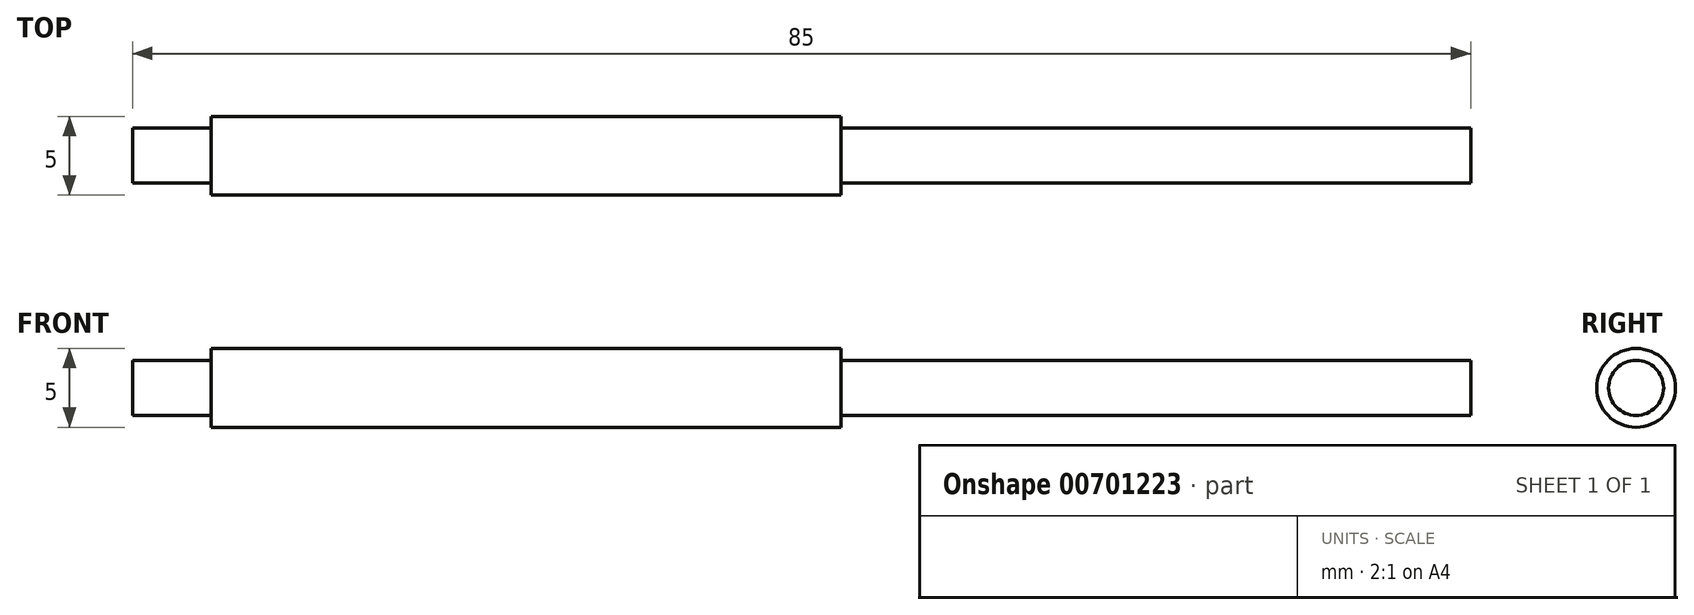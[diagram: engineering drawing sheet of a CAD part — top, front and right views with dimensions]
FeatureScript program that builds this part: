
annotation { "Feature Type Name" : "Feature", "Feature Type Description" : "" }
export const myFeature = defineFeature(function(context is Context, id is Id, definition is map)
    precondition{}
    {
        {
            var Q0;
            Q0=qCreatedBy(makeId("Top.planeOp"),FACE);
            var sketch = newSketch(context, id + "F0", { "sketchPlane" : qUnion([Q0])});
            skLineSegment(sketch, "E0.bottom", {"start": v(-20, 15) * mm, "end": v(20, 15) * mm});
            skLineSegment(sketch, "E0.top", {"start": v(-20, 0) * mm, "end": v(20, 0) * mm});
            skLineSegment(sketch, "E0.left", {"start": v(-20, 15) * mm, "end": v(-20, 0) * mm});
            skLineSegment(sketch, "E0.right", {"start": v(20, 15) * mm, "end": v(20, 0) * mm});
            skPoint(sketch, "E0.middle", {"position": v(0, 7.5) * mm});
            skSolve(sketch);
        }
        {
            var Q0;
            Q0=qSketchRegion(id+"F0",true);
            var Q1;
            Q1=sQuery(id+"F0.wireOp",EDGE,"E0.top");
            revolve(context, id + "F1", {"entities" : qUnion([Q0]), "axis" : qUnion([Q1]), "revolveType" : RevolveType.FULL});
        }
        {
            var Q0;
            Q0=makeQuery(id+"F1.opRevolve","SWEPT_FACE",FACE,{"disambiguationData":[OSD([sQuery(id+"F0.wireOp",EDGE,"E0.right")])]});
            var sketch = newSketch(context, id + "F2", { "sketchPlane" : qUnion([Q0])});
            skCircle(sketch, "E1", {"center": v(0, 0) * mm, "radius": 1.75 * mm});
            skCircle(sketch, "E2.0", {"center": v(0, 0) * mm, "radius": 15 * mm});
            skLineSegment(sketch, "E3", {"start": v(-10.07, -11.12) * mm, "end": v(-0.6, -1.65) * mm});
            skLineSegment(sketch, "E4", {"start": v(-11.13, -10.06) * mm, "end": v(-1.65, -0.58) * mm});
            skLineSegment(sketch, "E5", {"start": v(-14.98, 0.75) * mm, "end": v(-1.58, 0.75) * mm});
            skLineSegment(sketch, "E6", {"start": v(-14.98, -0.75) * mm, "end": v(-1.58, -0.75) * mm});
            skLineSegment(sketch, "E7", {"start": v(-0.75, 14.98) * mm, "end": v(-0.75, 1.58) * mm});
            skLineSegment(sketch, "E8", {"start": v(0.75, -14.98) * mm, "end": v(0.75, -1.58) * mm});
            skLineSegment(sketch, "E9.MirrorCS", {"start": v(-0.75, -14.98) * mm, "end": v(-0.75, -1.58) * mm});
            skLineSegment(sketch, "E10.MirrorCS", {"start": v(11.13, -10.06) * mm, "end": v(1.65, -0.58) * mm});
            skLineSegment(sketch, "E11.MirrorCS", {"start": v(10.07, -11.12) * mm, "end": v(0.6, -1.65) * mm});
            skCircle(sketch, "E12", {"center": v(0, 0) * mm, "radius": 2.5 * mm});
            skLineSegment(sketch, "E13.trimOffspring", {"start": v(-1.65, 0.6) * mm, "end": v(-11.12, 10.07) * mm});
            skLineSegment(sketch, "E14.trimOffspring", {"start": v(0.58, 1.65) * mm, "end": v(10.06, 11.13) * mm});
            skLineSegment(sketch, "E15.trimOffspring", {"start": v(1.58, 0.75) * mm, "end": v(14.98, 0.75) * mm});
            skLineSegment(sketch, "E16.trimOffspring", {"start": v(-0.75, 1.58) * mm, "end": v(-0.75, 14.98) * mm});
            skLineSegment(sketch, "E17.trimOffspring", {"start": v(-0.75, -1.58) * mm, "end": v(-0.75, -14.98) * mm});
            skLineSegment(sketch, "E18.trimOffspring", {"start": v(-0.58, 1.65) * mm, "end": v(-10.06, 11.13) * mm});
            skLineSegment(sketch, "E19.trimOffspring", {"start": v(0.75, 1.58) * mm, "end": v(0.75, 14.98) * mm});
            skLineSegment(sketch, "E20.trimOffspring", {"start": v(1.65, 0.6) * mm, "end": v(11.12, 10.07) * mm});
            skLineSegment(sketch, "E21.trimOffspring", {"start": v(1.58, -0.75) * mm, "end": v(14.98, -0.75) * mm});
            skSolve(sketch);
        }
        {
            var Q0;
            {var subQ0=sQuery(id+"F2.wireOp",EDGE,"E1");var subQ8=makeQuery(id+"F2.imprint","INTERSECT",VERTEX,{"derivedFrom":[subQ0,sQuery(id+"F2.wireOp",EDGE,"E15.trimOffspring")]});Q0=makeQuery(id+"F2.imprint","IMPRINT",FACE,{"disambiguationData":[TD([[makeQuery(id+"F2.imprint","IMPRINT",EDGE,{"disambiguationData":[TD([[subQ8,1.0]])],"derivedFrom":subQ0}),1.0]])]});}
            var Q1;
            {var subQ0=sQuery(id+"F2.wireOp",EDGE,"E15.trimOffspring");var subQ1=sQuery(id+"F2.wireOp",EDGE,"E2.0");var subQ2=makeQuery(id+"F2.imprint","INTERSECT",VERTEX,{"derivedFrom":[subQ1,subQ0]});Q1=makeQuery(id+"F2.imprint","IMPRINT",FACE,{"disambiguationData":[TD([[makeQuery(id+"F2.imprint","IMPRINT",EDGE,{"disambiguationData":[TD([[subQ2,1.0]])],"derivedFrom":subQ1}),-1.0]])]});}
            var Q2;
            {var subQ0=sQuery(id+"F2.wireOp",EDGE,"E10.MirrorCS");var subQ1=sQuery(id+"F2.wireOp",EDGE,"E2.0");var subQ2=makeQuery(id+"F2.imprint","INTERSECT",VERTEX,{"derivedFrom":[subQ1,subQ0]});Q2=makeQuery(id+"F2.imprint","IMPRINT",FACE,{"disambiguationData":[TD([[makeQuery(id+"F2.imprint","IMPRINT",EDGE,{"disambiguationData":[TD([[subQ2,1.0]])],"derivedFrom":subQ1}),-1.0]])]});}
            var Q3;
            {var subQ0=sQuery(id+"F2.wireOp",EDGE,"E8");var subQ1=sQuery(id+"F2.wireOp",EDGE,"E2.0");var subQ2=makeQuery(id+"F2.imprint","INTERSECT",VERTEX,{"derivedFrom":[subQ1,subQ0]});Q3=makeQuery(id+"F2.imprint","IMPRINT",FACE,{"disambiguationData":[TD([[makeQuery(id+"F2.imprint","IMPRINT",EDGE,{"disambiguationData":[TD([[subQ2,1.0]])],"derivedFrom":subQ1}),-1.0]])]});}
            var Q4;
            {var subQ0=sQuery(id+"F2.wireOp",EDGE,"E3");var subQ1=sQuery(id+"F2.wireOp",EDGE,"E2.0");var subQ2=makeQuery(id+"F2.imprint","INTERSECT",VERTEX,{"derivedFrom":[subQ1,subQ0]});Q4=makeQuery(id+"F2.imprint","IMPRINT",FACE,{"disambiguationData":[TD([[makeQuery(id+"F2.imprint","IMPRINT",EDGE,{"disambiguationData":[TD([[subQ2,1.0]])],"derivedFrom":subQ1}),-1.0]])]});}
            var Q5;
            {var subQ0=sQuery(id+"F2.wireOp",EDGE,"E4");var subQ1=sQuery(id+"F2.wireOp",EDGE,"E2.0");var subQ2=makeQuery(id+"F2.imprint","INTERSECT",VERTEX,{"derivedFrom":[subQ1,subQ0]});Q5=makeQuery(id+"F2.imprint","IMPRINT",FACE,{"disambiguationData":[TD([[makeQuery(id+"F2.imprint","IMPRINT",EDGE,{"disambiguationData":[TD([[subQ2,-1.0]])],"derivedFrom":subQ1}),-1.0]])]});}
            var Q6;
            {var subQ0=sQuery(id+"F2.wireOp",EDGE,"E5");var subQ1=sQuery(id+"F2.wireOp",EDGE,"E2.0");var subQ2=makeQuery(id+"F2.imprint","INTERSECT",VERTEX,{"derivedFrom":[subQ1,subQ0]});Q6=makeQuery(id+"F2.imprint","IMPRINT",FACE,{"disambiguationData":[TD([[makeQuery(id+"F2.imprint","IMPRINT",EDGE,{"disambiguationData":[TD([[subQ2,-1.0]])],"derivedFrom":subQ1}),-1.0]])]});}
            var Q7;
            {var subQ0=sQuery(id+"F2.wireOp",EDGE,"E16.trimOffspring");var subQ1=sQuery(id+"F2.wireOp",EDGE,"E2.0");var subQ2=makeQuery(id+"F2.imprint","INTERSECT",VERTEX,{"derivedFrom":[subQ1,subQ0]});Q7=makeQuery(id+"F2.imprint","IMPRINT",FACE,{"disambiguationData":[TD([[makeQuery(id+"F2.imprint","IMPRINT",EDGE,{"disambiguationData":[TD([[subQ2,1.0]])],"derivedFrom":subQ1}),-1.0]])]});}
            var Q8;
            {var subQ0=sQuery(id+"F2.wireOp",EDGE,"E14.trimOffspring");var subQ1=sQuery(id+"F2.wireOp",EDGE,"E2.0");var subQ2=makeQuery(id+"F2.imprint","INTERSECT",VERTEX,{"derivedFrom":[subQ1,subQ0]});Q8=makeQuery(id+"F2.imprint","IMPRINT",FACE,{"disambiguationData":[TD([[makeQuery(id+"F2.imprint","IMPRINT",EDGE,{"disambiguationData":[TD([[subQ2,1.0]])],"derivedFrom":subQ1}),-1.0]])]});}
            extrude(context, id + "F3", {"entities" : qUnion([Q0, Q1, Q2, Q3, Q4, Q5, Q6, Q7, Q8]), "operationType" : NewBodyOperationType.REMOVE, "endBound" : BoundingType.THROUGH_ALL, "oppositeDirection" : true, "depth" : 25 * mm, "offsetDistance" : 25 * mm});
        }
        {
            var Q0;
            Q0=makeQuery(id+"F1.opRevolve","SWEPT_FACE",FACE,{"disambiguationData":[OSD([sQuery(id+"F0.wireOp",EDGE,"E0.left")])]});
            var sketch = newSketch(context, id + "F4", { "sketchPlane" : qUnion([Q0])});
            skCircle(sketch, "E22", {"center": v(0, 0) * mm, "radius": 0.75 * mm});
            skSolve(sketch);
        }
        {
            var Q0;
            {var subQ2=sQuery(id+"F0.wireOp",EDGE,"E0.left");var subQ3=makeQuery(id+"F1.opRevolve","SWEPT_FACE",FACE,{"disambiguationData":[OSD([subQ2])]});Q0=makeQuery(id+"F4.imprint","IMPRINT",FACE,{"disambiguationData":[TD([[makeQuery(id+"F4.imprint","IMPRINT",EDGE,{"derivedFrom":makeQuery(id+"F3.boolean.opBoolean","INTERSECT",EDGE,{"derivedFrom":[subQ3,makeQuery(id+"F3.opExtrude","SWEPT_FACE",FACE,{"disambiguationData":[OSD([sQuery(id+"F2.wireOp",EDGE,"E1")])]})]})}),1.0]])]});}
            var sketch = newSketch(context, id + "F5", { "sketchPlane" : qUnion([Q0])});
            skCircle(sketch, "E23.0", {"center": v(0, 0) * mm, "radius": 1.75 * mm});
            skCircle(sketch, "E24.cCircle", {"center": v(0, 0) * mm, "radius": 1.75 * mm, "construction": true});
            skLineSegment(sketch, "E24.0", {"start": v(0.78, -1.57) * mm, "end": v(-1.75, 0.11) * mm});
            skLineSegment(sketch, "E24.1", {"start": v(-1.75, 0.11) * mm, "end": v(0.97, 1.46) * mm});
            skLineSegment(sketch, "E24.2", {"start": v(0.97, 1.46) * mm, "end": v(0.78, -1.57) * mm});
            skSolve(sketch);
        }
        {
            var Q0;
            Q0=makeQuery(id+"F4.imprint","IMPRINT",FACE,{"disambiguationData":[TD([[makeQuery(id+"F4.imprint","IMPRINT",EDGE,{"derivedFrom":sQuery(id+"F4.wireOp",EDGE,"E22")}),-1.0]])]});
            var Q1;
            Q1=makeQuery(id+"F4.imprint","IMPRINT",FACE,{"disambiguationData":[TD([[makeQuery(id+"F4.imprint","IMPRINT",EDGE,{"derivedFrom":sQuery(id+"F4.wireOp",EDGE,"E22")}),1.0]])]});
            var Q2;
            Q2=sQuery(id+"F5.wireOp",EDGE,"E23.0");
            extrude(context, id + "F6", {"entities" : qUnion([Q0, Q1]), "operationType" : NewBodyOperationType.ADD, "surfaceEntities" : qUnion([Q2]), "depth" : 5 * mm, "offsetDistance" : 25 * mm, "hasSecondDirection" : true, "secondDirectionOppositeDirection" : true, "secondDirectionDepth" : 80 * mm});
        }
    });
